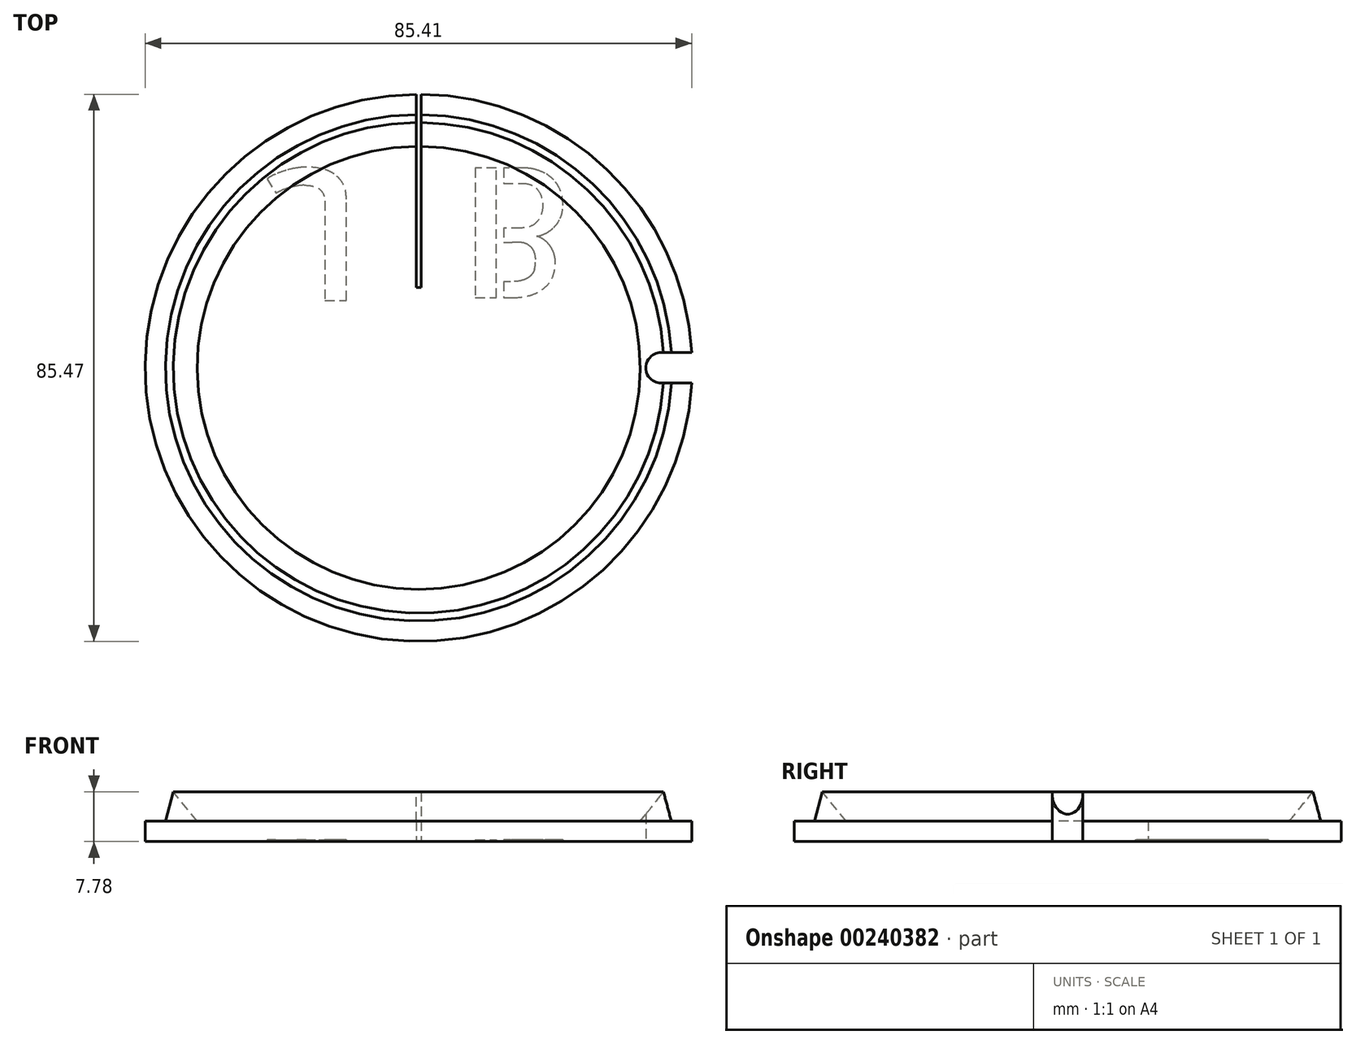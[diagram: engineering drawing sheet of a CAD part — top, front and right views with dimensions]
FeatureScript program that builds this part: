
annotation { "Feature Type Name" : "Feature", "Feature Type Description" : "" }
export const myFeature = defineFeature(function(context is Context, id is Id, definition is map)
    precondition{}
    {
        {
            var Q0;
            Q0=qCreatedBy(makeId("Front.planeOp"),FACE);
            var sketch = newSketch(context, id + "F0", { "sketchPlane" : qUnion([Q0])});
            skLineSegment(sketch, "E0", {"start": v(0, 0) * mm, "end": v(42.74, 0) * mm});
            skLineSegment(sketch, "E1", {"start": v(42.74, 0) * mm, "end": v(42.74, 3.18) * mm});
            skLineSegment(sketch, "E2", {"start": v(42.74, 3.18) * mm, "end": v(39.56, 3.18) * mm});
            skLineSegment(sketch, "E3", {"start": v(39.56, 3.18) * mm, "end": v(38.33, 7.78) * mm});
            skLineSegment(sketch, "E4", {"start": v(38.33, 7.78) * mm, "end": v(34.62, 3.17) * mm});
            skLineSegment(sketch, "E5", {"start": v(34.62, 3.18) * mm, "end": v(0, 3.18) * mm});
            skLineSegment(sketch, "E6", {"start": v(0, 3.18) * mm, "end": v(0, 0) * mm});
            skLineSegment(sketch, "E7", {"start": v(0, 0) * mm, "end": v(0, -12.54) * mm, "construction": true});
            skSolve(sketch);
        }
        {
            var Q0;
            Q0=makeQuery(id+"F0.imprint","IMPRINT",FACE,{"disambiguationData":[TD([[makeQuery(id+"F0.imprint","IMPRINT",EDGE,{"derivedFrom":sQuery(id+"F0.wireOp",EDGE,"E0")}),1.0]])]});
            var Q1;
            Q1=sQuery(id+"F0.wireOp",EDGE,"E7");
            revolve(context, id + "F1", {"entities" : qUnion([Q0]), "axis" : qUnion([Q1]), "revolveType" : RevolveType.FULL});
        }
        {
            var Q0;
            Q0=makeQuery(id+"F1.opRevolve","SWEPT_FACE",FACE,{"disambiguationData":[OSD([sQuery(id+"F0.wireOp",EDGE,"E0")])]});
            var sketch = newSketch(context, id + "F2", { "sketchPlane" : qUnion([Q0])});
            skArc(sketch, "E8", {"start": v(37.9, 2.39) * mm, "mid": v(35.5, 0) * mm, "end": v(37.9, -2.39) * mm});
            skLineSegment(sketch, "E9", {"start": v(37.9, 2.39) * mm, "end": v(42.67, 2.39) * mm});
            skLineSegment(sketch, "E10", {"start": v(37.9, -2.39) * mm, "end": v(42.67, -2.39) * mm});
            skArc(sketch, "E11.0", {"start": v(42.67, -2.39) * mm, "mid": v(42.74, 0) * mm, "end": v(42.67, 2.39) * mm});
            skSolve(sketch);
        }
        {
            var Q0;
            Q0=makeQuery(id+"F2.imprint","IMPRINT",FACE,{"disambiguationData":[TD([[makeQuery(id+"F2.imprint","IMPRINT",EDGE,{"derivedFrom":sQuery(id+"F2.wireOp",EDGE,"E8")}),1.0]])]});
            extrude(context, id + "F3", {"entities" : qUnion([Q0]), "operationType" : NewBodyOperationType.REMOVE, "endBound" : BoundingType.THROUGH_ALL, "oppositeDirection" : true, "depth" : 25.4 * mm});
        }
        {
            var Q0;
            Q0=makeQuery(id+"F1.opRevolve","SWEPT_FACE",FACE,{"disambiguationData":[OSD([sQuery(id+"F0.wireOp",EDGE,"E0")])]});
            var sketch = newSketch(context, id + "F4", { "sketchPlane" : qUnion([Q0])});
            skLineSegment(sketch, "E12.bottom", {"start": v(0.38, -12.56) * mm, "end": v(-0.38, -12.56) * mm});
            skLineSegment(sketch, "E12.top", {"start": v(0.38, -72.91) * mm, "end": v(-0.38, -72.91) * mm});
            skLineSegment(sketch, "E12.left", {"start": v(0.38, -12.56) * mm, "end": v(0.38, -72.91) * mm});
            skLineSegment(sketch, "E12.right", {"start": v(-0.38, -12.56) * mm, "end": v(-0.38, -72.91) * mm});
            skPoint(sketch, "E12.middle", {"position": v(0, -42.74) * mm});
            skSolve(sketch);
        }
        {
            var Q0;
            {var subQ0=sQuery(id+"F4.wireOp",EDGE,"E12.bottom");Q0=makeQuery(id+"F4.imprint","IMPRINT",FACE,{"disambiguationData":[TD([[makeQuery(id+"F4.imprint","IMPRINT",EDGE,{"derivedFrom":subQ0}),1.0]])]});}
            extrude(context, id + "F5", {"entities" : qUnion([Q0]), "operationType" : NewBodyOperationType.REMOVE, "endBound" : BoundingType.THROUGH_ALL, "oppositeDirection" : true, "depth" : 25.4 * mm});
        }
        {
            var Q0;
            Q0=makeQuery(id+"F1.opRevolve","SWEPT_FACE",FACE,{"disambiguationData":[OSD([sQuery(id+"F0.wireOp",EDGE,"E0")])]});
            var sketch = newSketch(context, id + "F6", { "sketchPlane" : qUnion([Q0])});
            skText(sketch, "E13", { "text": "J  B", "fontName": "AllertaStencil-Regular.ttf"});
            const initialGuessF6  = {"E13": [-0.02442, -0.03123, 1, 0, 0.02028]};
            skSetInitialGuess(sketch, initialGuessF6);
            skSolve(sketch);
        }
        {
            var Q0;
            Q0=makeQuery(id+"F6.imprint","IMPRINT",FACE,{"disambiguationData":[TD([[makeQuery(id+"F6.imprint","IMPRINT",EDGE,{"derivedFrom":sQuery(id+"F6.wireOp",EDGE,"E13.sketch_text.stroke-0")}),-1.0]])]});
            var Q1;
            Q1=makeQuery(id+"F6.imprint","IMPRINT",FACE,{"disambiguationData":[TD([[makeQuery(id+"F6.imprint","IMPRINT",EDGE,{"derivedFrom":sQuery(id+"F6.wireOp",EDGE,"E13.sketch_text.stroke-57")}),-1.0]])]});
            var Q2;
            Q2=makeQuery(id+"F6.imprint","IMPRINT",FACE,{"disambiguationData":[TD([[makeQuery(id+"F6.imprint","IMPRINT",EDGE,{"derivedFrom":sQuery(id+"F6.wireOp",EDGE,"E13.sketch_text.stroke-18")}),-1.0]])]});
            extrude(context, id + "F7", {"entities" : qUnion([Q0, Q1, Q2]), "operationType" : NewBodyOperationType.REMOVE, "oppositeDirection" : true, "depth" : .3 * mm});
        }
    });
